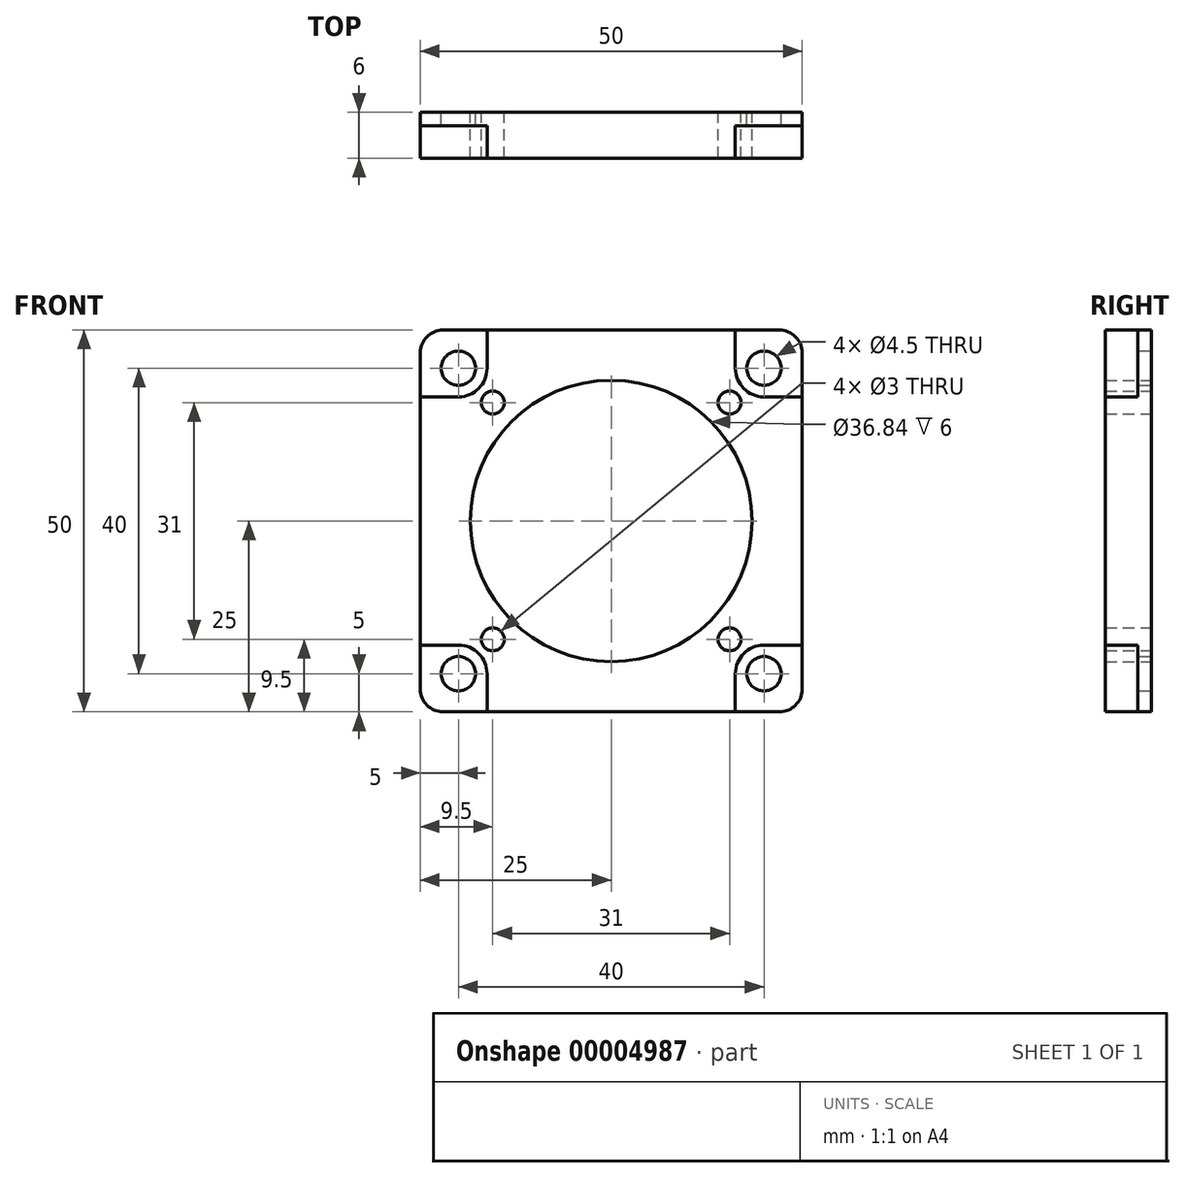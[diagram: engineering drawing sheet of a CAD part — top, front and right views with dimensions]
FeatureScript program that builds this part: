
annotation { "Feature Type Name" : "Feature", "Feature Type Description" : "" }
export const myFeature = defineFeature(function(context is Context, id is Id, definition is map)
    precondition{}
    {
        {
            var Q0;
            Q0=qCreatedBy(makeId("Front.planeOp"),FACE);
            var sketch = newSketch(context, id + "F0", { "sketchPlane" : qUnion([Q0])});
            skLineSegment(sketch, "E0.rect.bottom", {"start": v(25, 25) * mm, "end": v(-25, 25) * mm});
            skLineSegment(sketch, "E0.rect.top", {"start": v(25, -25) * mm, "end": v(-25, -25) * mm});
            skLineSegment(sketch, "E0.rect.left", {"start": v(25, 25) * mm, "end": v(25, -25) * mm});
            skLineSegment(sketch, "E0.rect.right", {"start": v(-25, 25) * mm, "end": v(-25, -25) * mm});
            skPoint(sketch, "E0.rect.middle", {"position": v(0, 0) * mm});
            skLineSegment(sketch, "E1", {"start": v(-25, 25) * mm, "end": v(0, 0) * mm, "construction": true});
            skCircle(sketch, "E2", {"center": v(-15.5, 15.5) * mm, "radius": 1.5 * mm});
            skCircle(sketch, "E3", {"center": v(-20, 20) * mm, "radius": 2.25 * mm});
            skCircle(sketch, "E4", {"center": v(0, 0) * mm, "radius": 18.42 * mm});
            skPoint(sketch, "E5", {"position": v(-14.44, 14.44) * mm});
            skCircle(sketch, "E6", {"center": v(-20, 20) * mm, "radius": 3.4 * mm, "construction": true});
            skCircle(sketch, "E7.1.0", {"center": v(-20, -20) * mm, "radius": 2.25 * mm});
            skCircle(sketch, "E7.1.1", {"center": v(-15.5, -15.5) * mm, "radius": 1.5 * mm});
            skCircle(sketch, "E7.2.0", {"center": v(20, -20) * mm, "radius": 2.25 * mm});
            skCircle(sketch, "E7.2.1", {"center": v(15.5, -15.5) * mm, "radius": 1.5 * mm});
            skCircle(sketch, "E7.3.0", {"center": v(20, 20) * mm, "radius": 2.25 * mm});
            skCircle(sketch, "E7.3.1", {"center": v(15.5, 15.5) * mm, "radius": 1.5 * mm});
            skSolve(sketch);
        }
        {
            var Q0;
            Q0 = qSketchRegion(id + "F0", true);
            extrude(context, id + "F1", {"entities" : qUnion([Q0]), "depth" : 6 * mm});
        }
        {
            var Q0;
            Q0=makeQuery(id+"F1.opExtrude","CAP_FACE",FACE,{"disambiguationData":[OSD([sQuery(id+"F0.wireOp",EDGE,"E0.rect.bottom"),sQuery(id+"F0.wireOp",EDGE,"E0.rect.top"),sQuery(id+"F0.wireOp",EDGE,"E0.rect.left"),sQuery(id+"F0.wireOp",EDGE,"E0.rect.right"),sQuery(id+"F0.wireOp",EDGE,"E2"),sQuery(id+"F0.wireOp",EDGE,"E3"),sQuery(id+"F0.wireOp",EDGE,"E4"),sQuery(id+"F0.wireOp",EDGE,"E7.1.0"),sQuery(id+"F0.wireOp",EDGE,"E7.1.1"),sQuery(id+"F0.wireOp",EDGE,"E7.2.0"),sQuery(id+"F0.wireOp",EDGE,"E7.2.1"),sQuery(id+"F0.wireOp",EDGE,"E7.3.0"),sQuery(id+"F0.wireOp",EDGE,"E7.3.1")])],"isStart":false});
            var sketch = newSketch(context, id + "F2", { "sketchPlane" : qUnion([Q0])});
            skArc(sketch, "E8", {"start": v(-20, 16.25) * mm, "mid": v(-17.35, 17.35) * mm, "end": v(-16.25, 20) * mm});
            skLineSegment(sketch, "E9", {"start": v(-16.25, 20) * mm, "end": v(-16.25, 25) * mm});
            skLineSegment(sketch, "E10", {"start": v(-20, 16.25) * mm, "end": v(-25, 16.25) * mm});
            skLineSegment(sketch, "E11", {"start": v(-16.25, 25) * mm, "end": v(-25, 25) * mm});
            skLineSegment(sketch, "E12", {"start": v(-25, 25) * mm, "end": v(-25, 16.25) * mm});
            skLineSegment(sketch, "E13.1.0", {"start": v(-25, -16.25) * mm, "end": v(-25, -25) * mm});
            skArc(sketch, "E13.1.1", {"start": v(-16.25, -20) * mm, "mid": v(-17.35, -17.35) * mm, "end": v(-20, -16.25) * mm});
            skLineSegment(sketch, "E13.1.2", {"start": v(-16.25, -20) * mm, "end": v(-16.25, -25) * mm});
            skLineSegment(sketch, "E13.1.3", {"start": v(-25, -25) * mm, "end": v(-16.25, -25) * mm});
            skLineSegment(sketch, "E13.1.4", {"start": v(-20, -16.25) * mm, "end": v(-25, -16.25) * mm});
            skLineSegment(sketch, "E13.2.0", {"start": v(16.25, -25) * mm, "end": v(25, -25) * mm});
            skArc(sketch, "E13.2.1", {"start": v(20, -16.25) * mm, "mid": v(17.35, -17.35) * mm, "end": v(16.25, -20) * mm});
            skLineSegment(sketch, "E13.2.2", {"start": v(20, -16.25) * mm, "end": v(25, -16.25) * mm});
            skLineSegment(sketch, "E13.2.3", {"start": v(25, -25) * mm, "end": v(25, -16.25) * mm});
            skLineSegment(sketch, "E13.2.4", {"start": v(16.25, -20) * mm, "end": v(16.25, -25) * mm});
            skLineSegment(sketch, "E13.3.0", {"start": v(25, 16.25) * mm, "end": v(25, 25) * mm});
            skArc(sketch, "E13.3.1", {"start": v(16.25, 20) * mm, "mid": v(17.35, 17.35) * mm, "end": v(20, 16.25) * mm});
            skLineSegment(sketch, "E13.3.2", {"start": v(16.25, 20) * mm, "end": v(16.25, 25) * mm});
            skLineSegment(sketch, "E13.3.3", {"start": v(25, 25) * mm, "end": v(16.25, 25) * mm});
            skLineSegment(sketch, "E13.3.4", {"start": v(20, 16.25) * mm, "end": v(25, 16.25) * mm});
            skPoint(sketch, "E13.center", {"position": v(0, 0) * mm});
            skSolve(sketch);
        }
        {
            var Q0;
            Q0 = qSketchRegion(id + "F2", true);
            extrude(context, id + "F3", {"entities" : qUnion([Q0]), "operationType" : NewBodyOperationType.REMOVE, "oppositeDirection" : true, "depth" : 4.25 * mm});
        }
        {
            var Q0;
            Q0=makeQuery(id+"F1.opExtrude","SWEPT_EDGE",EDGE,{"disambiguationData":[OSD([sQuery(id+"F0.wireOp",EDGE,"E0.rect.bottom"),sQuery(id+"F0.wireOp",EDGE,"E0.rect.left")])]});
            var Q1;
            Q1=makeQuery(id+"F1.opExtrude","SWEPT_EDGE",EDGE,{"disambiguationData":[OSD([sQuery(id+"F0.wireOp",EDGE,"E0.rect.bottom"),sQuery(id+"F0.wireOp",EDGE,"E0.rect.right")])]});
            var Q2;
            Q2=makeQuery(id+"F1.opExtrude","SWEPT_EDGE",EDGE,{"disambiguationData":[OSD([sQuery(id+"F0.wireOp",EDGE,"E0.rect.top"),sQuery(id+"F0.wireOp",EDGE,"E0.rect.right")])]});
            var Q3;
            Q3=makeQuery(id+"F1.opExtrude","SWEPT_EDGE",EDGE,{"disambiguationData":[OSD([sQuery(id+"F0.wireOp",EDGE,"E0.rect.top"),sQuery(id+"F0.wireOp",EDGE,"E0.rect.left")])]});
            var Q4;
            Q4=makeQuery(id+"F3.boolean.opBoolean","COPY",EDGE,{"derivedFrom":makeQuery(id+"F3.opExtrude","SWEPT_EDGE",EDGE,{"disambiguationData":[OSD([sQuery(id+"F0.wireOp",EDGE,"E0.rect.top"),sQuery(id+"F2.wireOp",EDGE,"E13.2.0"),sQuery(id+"F2.wireOp",EDGE,"E13.2.4")])]})});
            var Q5;
            Q5=makeQuery(id+"F3.boolean.opBoolean","COPY",EDGE,{"derivedFrom":makeQuery(id+"F3.opExtrude","SWEPT_EDGE",EDGE,{"disambiguationData":[OSD([sQuery(id+"F0.wireOp",EDGE,"E0.rect.left"),sQuery(id+"F2.wireOp",EDGE,"E13.2.2"),sQuery(id+"F2.wireOp",EDGE,"E13.2.3")])]})});
            var Q6;
            Q6=makeQuery(id+"F3.boolean.opBoolean","COPY",EDGE,{"derivedFrom":makeQuery(id+"F3.opExtrude","SWEPT_EDGE",EDGE,{"disambiguationData":[OSD([sQuery(id+"F0.wireOp",EDGE,"E0.rect.top"),sQuery(id+"F2.wireOp",EDGE,"E13.1.2"),sQuery(id+"F2.wireOp",EDGE,"E13.1.3")])]})});
            var Q7;
            Q7=makeQuery(id+"F3.boolean.opBoolean","COPY",EDGE,{"derivedFrom":makeQuery(id+"F3.opExtrude","SWEPT_EDGE",EDGE,{"disambiguationData":[OSD([sQuery(id+"F0.wireOp",EDGE,"E0.rect.right"),sQuery(id+"F2.wireOp",EDGE,"E13.1.0"),sQuery(id+"F2.wireOp",EDGE,"E13.1.4")])]})});
            var Q8;
            Q8=makeQuery(id+"F3.boolean.opBoolean","COPY",EDGE,{"derivedFrom":makeQuery(id+"F3.opExtrude","SWEPT_EDGE",EDGE,{"disambiguationData":[OSD([sQuery(id+"F0.wireOp",EDGE,"E0.rect.right"),sQuery(id+"F2.wireOp",EDGE,"E10"),sQuery(id+"F2.wireOp",EDGE,"E12")])]})});
            var Q9;
            Q9=makeQuery(id+"F3.boolean.opBoolean","COPY",EDGE,{"derivedFrom":makeQuery(id+"F3.opExtrude","SWEPT_EDGE",EDGE,{"disambiguationData":[OSD([sQuery(id+"F0.wireOp",EDGE,"E0.rect.bottom"),sQuery(id+"F2.wireOp",EDGE,"E9"),sQuery(id+"F2.wireOp",EDGE,"E11")])]})});
            var Q10;
            Q10=makeQuery(id+"F3.boolean.opBoolean","COPY",EDGE,{"derivedFrom":makeQuery(id+"F3.opExtrude","SWEPT_EDGE",EDGE,{"disambiguationData":[OSD([sQuery(id+"F0.wireOp",EDGE,"E0.rect.bottom"),sQuery(id+"F2.wireOp",EDGE,"E13.3.2"),sQuery(id+"F2.wireOp",EDGE,"E13.3.3")])]})});
            var Q11;
            Q11=makeQuery(id+"F3.boolean.opBoolean","COPY",EDGE,{"derivedFrom":makeQuery(id+"F3.opExtrude","SWEPT_EDGE",EDGE,{"disambiguationData":[OSD([sQuery(id+"F0.wireOp",EDGE,"E0.rect.left"),sQuery(id+"F2.wireOp",EDGE,"E13.3.0"),sQuery(id+"F2.wireOp",EDGE,"E13.3.4")])]})});
            fillet(context, id + "F4", {"entities" : qUnion([Q0, Q1, Q2, Q3, Q4, Q5, Q6, Q7, Q8, Q9, Q10, Q11]), "radius" : 3 * mm, "tangentPropagation" : true, "allowEdgeOverflow" : false});
        }
    });
